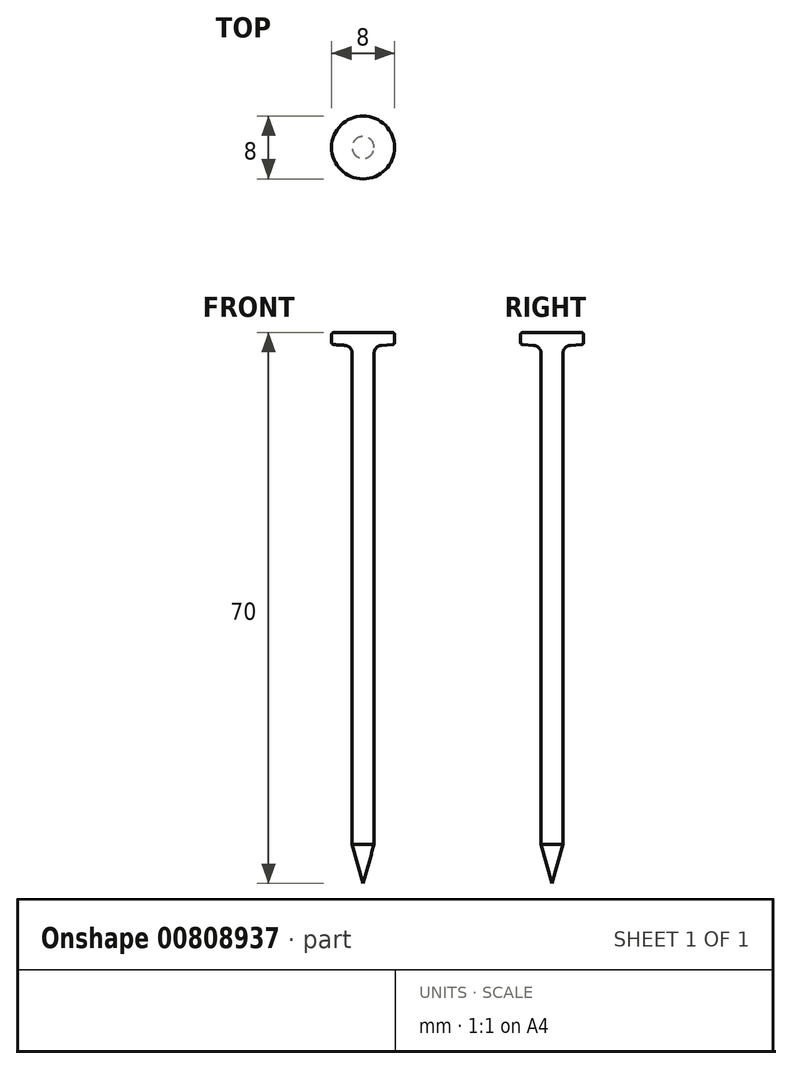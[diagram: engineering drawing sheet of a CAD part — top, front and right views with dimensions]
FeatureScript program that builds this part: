
annotation { "Feature Type Name" : "Feature", "Feature Type Description" : "" }
export const myFeature = defineFeature(function(context is Context, id is Id, definition is map)
    precondition{}
    {
        {
            var Q0;
            Q0=qCreatedBy(makeId("Front.planeOp"),FACE);
            var sketch = newSketch(context, id + "F0", { "sketchPlane" : qUnion([Q0])});
            skLineSegment(sketch, "E0", {"start": v(0, 0) * mm, "end": v(0, -70) * mm});
            skLineSegment(sketch, "E1", {"start": v(0, -70) * mm, "end": v(-1.4, -65) * mm});
            skLineSegment(sketch, "E2", {"start": v(-1.4, -65) * mm, "end": v(-1.4, 0) * mm});
            skLineSegment(sketch, "E3", {"start": v(-1.4, 0) * mm, "end": v(0, 0) * mm});
            skLineSegment(sketch, "E4", {"start": v(0, 0) * mm, "end": v(-4, 0) * mm});
            skLineSegment(sketch, "E5", {"start": v(-4, 0) * mm, "end": v(-4, -1.52) * mm});
            skLineSegment(sketch, "E6", {"start": v(-4, -1.52) * mm, "end": v(-1.4, -1.69) * mm});
            skSolve(sketch);
        }
        {
            var Q0;
            {var subQ3=sQuery(id+"F0.wireOp",EDGE,"yz4U7bQy-fufg-4PhD-KFNS-TyFrTUNHEGdd");Q0=makeQuery(id+"F0.imprint","IMPRINT",FACE,{"disambiguationData":[TD([[makeQuery(id+"F0.imprint","IMPRINT",EDGE,{"derivedFrom":subQ3}),1.0]])]});}
            var Q1;
            {var subQ0=sQuery(id+"F0.wireOp",EDGE,"E0");Q1=makeQuery(id+"F0.imprint","IMPRINT",FACE,{"disambiguationData":[TD([[makeQuery(id+"F0.imprint","IMPRINT",EDGE,{"derivedFrom":subQ0}),-1.0]])]});}
            var Q2;
            {var subQ4=sQuery(id+"F0.wireOp",EDGE,"lSyIZ4Td-KzSl-kbcH-Kt7I-iV4zs0mA5W3V");Q2=makeQuery(id+"F0.imprint","IMPRINT",FACE,{"disambiguationData":[TD([[makeQuery(id+"F0.imprint","IMPRINT",EDGE,{"derivedFrom":subQ4}),1.0]])]});}
            var Q3;
            {var subQ4=sQuery(id+"F0.wireOp",EDGE,"E5");Q3=makeQuery(id+"F0.imprint","IMPRINT",FACE,{"disambiguationData":[TD([[makeQuery(id+"F0.imprint","IMPRINT",EDGE,{"derivedFrom":subQ4}),1.0]])]});}
            var Q4;
            Q4=sQuery(id+"F0.wireOp",EDGE,"phutvW9v-odYo-YKQ7-GWsg-PvlayN9kfJxq");
            var Q5;
            Q5=sQuery(id+"F0.wireOp",EDGE,"yz4U7bQy-fufg-4PhD-KFNS-TyFrTUNHEGdd");
            var Q6;
            Q6=sQuery(id+"F0.wireOp",EDGE,"E2");
            var Q7;
            Q7=sQuery(id+"F0.wireOp",EDGE,"E4");
            var Q8;
            Q8=sQuery(id+"F0.wireOp",EDGE,"E3");
            var Q9;
            Q9=sQuery(id+"F0.wireOp",EDGE,"E1");
            var Q10;
            Q10=sQuery(id+"F0.wireOp",EDGE,"E0");
            var Q11;
            Q11=sQuery(id+"F0.wireOp",EDGE,"E0");
            revolve(context, id + "F1", {"surfaceOperationType" : NewSurfaceOperationType.NEW, "entities" : qUnion([Q0, Q1, Q2, Q3]), "surfaceEntities" : qUnion([Q4, Q5, Q6, Q7, Q8, Q9, Q10]), "axis" : qUnion([Q11]), "revolveType" : RevolveType.FULL});
        }
        {
            var Q0;
            Q0=makeQuery(id+"F1.opRevolve","SWEPT_EDGE",EDGE,{"disambiguationData":[OSD([sQuery(id+"F0.wireOp",EDGE,"E2"),sQuery(id+"F0.wireOp",EDGE,"E6")])]});
            fillet(context, id + "F2", {"entities" : qUnion([Q0]), "radius" : 1 * mm, "tangentPropagation" : true, "allowEdgeOverflow" : false});
        }
        {
            var Q0;
            Q0=makeQuery(id+"F1.opRevolve","SWEPT_EDGE",EDGE,{"disambiguationData":[OSD([sQuery(id+"F0.wireOp",EDGE,"E4"),sQuery(id+"F0.wireOp",EDGE,"E5")])]});
            var Q1;
            Q1=makeQuery(id+"F1.opRevolve","SWEPT_EDGE",EDGE,{"disambiguationData":[OSD([sQuery(id+"F0.wireOp",EDGE,"E5"),sQuery(id+"F0.wireOp",EDGE,"E6")])]});
            fillet(context, id + "F3", {"entities" : qUnion([Q0, Q1]), "radius" : 0.3 * mm, "tangentPropagation" : true, "allowEdgeOverflow" : false});
        }
    });
